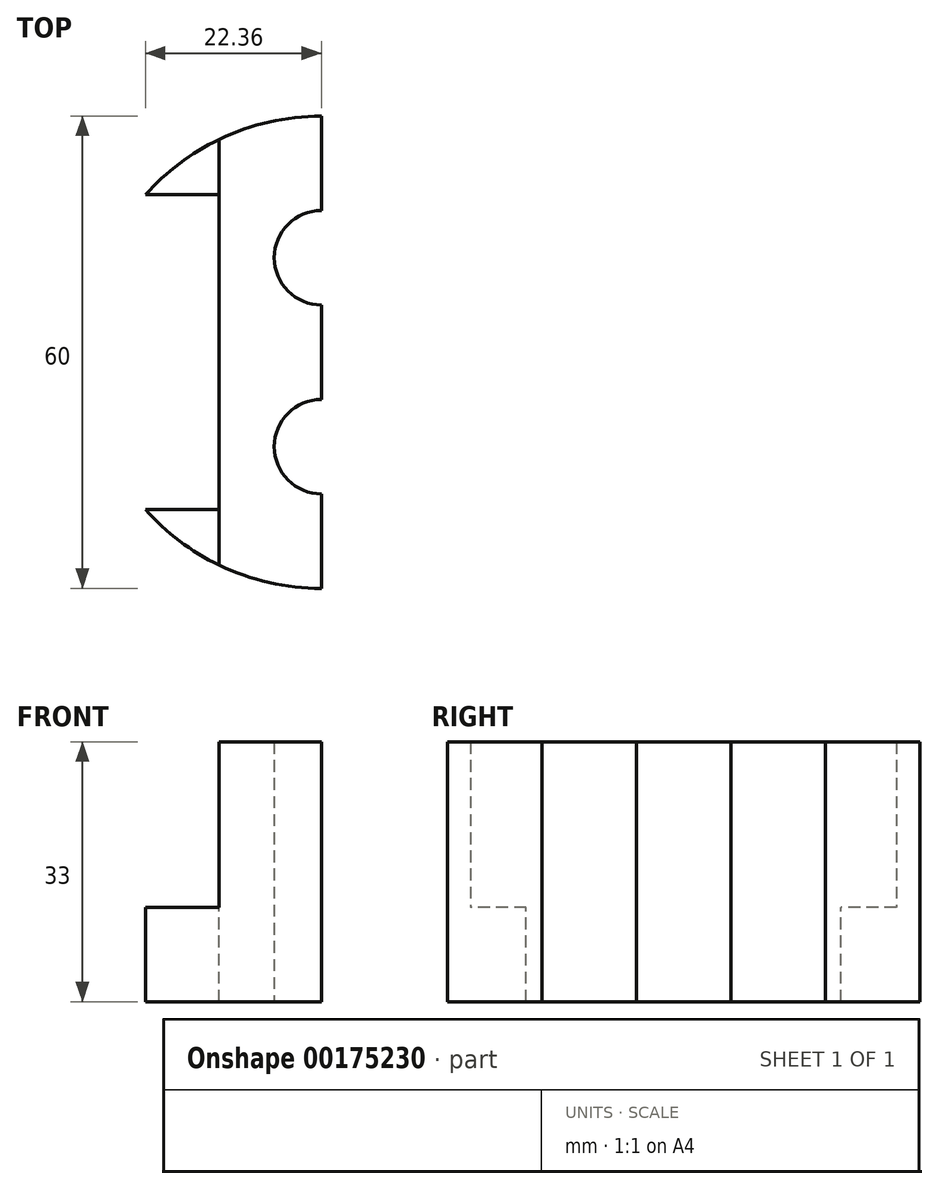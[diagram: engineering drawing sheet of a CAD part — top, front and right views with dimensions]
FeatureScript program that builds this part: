
annotation { "Feature Type Name" : "Feature", "Feature Type Description" : "" }
export const myFeature = defineFeature(function(context is Context, id is Id, definition is map)
    precondition{}
    {
        {
            var Q0;
            Q0=qCreatedBy(makeId("Top.planeOp"),FACE);
            var sketch = newSketch(context, id + "F0", { "sketchPlane" : qUnion([Q0])});
            skLineSegment(sketch, "E0.bottom", {"start": v(-13, -12) * mm, "end": v(13, -12) * mm});
            skLineSegment(sketch, "E0.top", {"start": v(-13, 12) * mm, "end": v(13, 12) * mm});
            skLineSegment(sketch, "E0.left", {"start": v(-13, -12) * mm, "end": v(-13, 12) * mm});
            skLineSegment(sketch, "E0.right", {"start": v(13, -12) * mm, "end": v(13, 12) * mm});
            skPoint(sketch, "E0.middle", {"position": v(0, 0) * mm});
            skCircle(sketch, "E1", {"center": v(0, 0) * mm, "radius": 20 * mm, "construction": true});
            skLineSegment(sketch, "E2", {"start": v(-31.1, 0) * mm, "end": v(39.02, 0) * mm, "construction": true});
            skCircle(sketch, "E3", {"center": v(0, 0) * mm, "radius": 30 * mm});
            skCircle(sketch, "E4", {"center": v(0, 12) * mm, "radius": 6 * mm});
            skCircle(sketch, "E5", {"center": v(0, -12) * mm, "radius": 6 * mm});
            skLineSegment(sketch, "E6.bottom", {"start": v(-13, 27.04) * mm, "end": v(13, 27.04) * mm});
            skLineSegment(sketch, "E6.top", {"start": v(-13, -27.04) * mm, "end": v(13, -27.04) * mm});
            skLineSegment(sketch, "E6.left", {"start": v(-13, 27.04) * mm, "end": v(-13, -27.04) * mm});
            skLineSegment(sketch, "E6.right", {"start": v(13, 27.04) * mm, "end": v(13, -27.04) * mm});
            skSolve(sketch);
        }
        {
            var Q0;
            {var subQ0=sQuery(id+"F0.wireOp",EDGE,"E6.bottom");Q0=makeQuery(id+"F0.imprint","IMPRINT",FACE,{"disambiguationData":[TD([[makeQuery(id+"F0.imprint","IMPRINT",EDGE,{"derivedFrom":subQ0}),1.0]])]});}
            var Q1;
            {var subQ0=sQuery(id+"F0.wireOp",EDGE,"E6.top");Q1=makeQuery(id+"F0.imprint","IMPRINT",FACE,{"disambiguationData":[TD([[makeQuery(id+"F0.imprint","IMPRINT",EDGE,{"derivedFrom":subQ0}),-1.0]])]});}
            var Q2;
            {var subQ0=sQuery(id+"F0.wireOp",EDGE,"E6.top");Q2=makeQuery(id+"F0.imprint","IMPRINT",FACE,{"disambiguationData":[TD([[makeQuery(id+"F0.imprint","IMPRINT",EDGE,{"derivedFrom":subQ0}),1.0]])]});}
            var Q3;
            {var subQ6=sQuery(id+"F0.wireOp",EDGE,"E0.bottom");var subQ9=sQuery(id+"F0.wireOp",EDGE,"E6.left");var subQ13=makeQuery(id+"F0.imprint","INTERSECT",VERTEX,{"derivedFrom":[subQ6,subQ9]});Q3=makeQuery(id+"F0.imprint","IMPRINT",FACE,{"disambiguationData":[TD([[makeQuery(id+"F0.imprint","IMPRINT",EDGE,{"disambiguationData":[TD([[subQ13,-1.0]])],"derivedFrom":subQ6}),1.0]])]});}
            var Q4;
            {var subQ0=sQuery(id+"F0.wireOp",EDGE,"E6.bottom");Q4=makeQuery(id+"F0.imprint","IMPRINT",FACE,{"disambiguationData":[TD([[makeQuery(id+"F0.imprint","IMPRINT",EDGE,{"derivedFrom":subQ0}),-1.0]])]});}
            extrude(context, id + "F1", {"entities" : qUnion([Q0, Q1, Q2, Q3, Q4]), "depth" : 33 * mm});
        }
        {
            var Q0;
            Q0=qCreatedBy(makeId("Top.planeOp"),FACE);
            var sketch = newSketch(context, id + "F2", { "sketchPlane" : qUnion([Q0])});
            skCircle(sketch, "E7", {"center": v(0, 0) * mm, "radius": 30 * mm});
            skCircle(sketch, "E8", {"center": v(-26.68, -13.72) * mm, "radius": 7.63 * mm});
            skLineSegment(sketch, "E9", {"start": v(-22.36, -20) * mm, "end": v(-12.88, -20) * mm});
            skLineSegment(sketch, "E10", {"start": v(-12.88, -20) * mm, "end": v(22.36, -20) * mm});
            skLineSegment(sketch, "E11", {"start": v(22.36, -20) * mm, "end": v(-53.5, 0) * mm, "construction": true});
            skLineSegment(sketch, "E12", {"start": v(-53.5, 0) * mm, "end": v(57.64, 0) * mm, "construction": true});
            skLineSegment(sketch, "E13.MirrorCS", {"start": v(-12.88, 20) * mm, "end": v(22.36, 20) * mm});
            skLineSegment(sketch, "E14.MirrorCS", {"start": v(-22.36, 20) * mm, "end": v(-12.88, 20) * mm});
            skSolve(sketch);
        }
        {
            var Q0;
            {var subQ0=sQuery(id+"F2.wireOp",EDGE,"E13.MirrorCS");Q0=makeQuery(id+"F2.imprint","IMPRINT",FACE,{"disambiguationData":[TD([[makeQuery(id+"F2.imprint","IMPRINT",EDGE,{"derivedFrom":subQ0}),1.0]])]});}
            var Q1;
            {var subQ0=sQuery(id+"F2.wireOp",EDGE,"E9");Q1=makeQuery(id+"F2.imprint","IMPRINT",FACE,{"disambiguationData":[TD([[makeQuery(id+"F2.imprint","IMPRINT",EDGE,{"derivedFrom":subQ0}),-1.0]])]});}
            extrude(context, id + "F3", {"entities" : qUnion([Q0, Q1]), "operationType" : NewBodyOperationType.ADD, "depth" : 12 * mm});
        }
        {
            var Q0;
            Q0=makeQuery(id+"F1.opExtrude","CAP_FACE",FACE,{"disambiguationData":[OSD([sQuery(id+"F0.wireOp",EDGE,"E3"),sQuery(id+"F0.wireOp",EDGE,"E4"),sQuery(id+"F0.wireOp",EDGE,"E5"),sQuery(id+"F0.wireOp",EDGE,"E6.left"),sQuery(id+"F0.wireOp",EDGE,"E6.right")])],"isStart":false});
            var sketch = newSketch(context, id + "F4", { "sketchPlane" : qUnion([Q0])});
            skLineSegment(sketch, "E15", {"start": v(0, 35.89) * mm, "end": v(0, -37.95) * mm});
            skPoint(sketch, "E15.endSnap0", {"position": v(0, 30) * mm});
            skLineSegment(sketch, "E16", {"start": v(0, -37.95) * mm, "end": v(28.6, -37.95) * mm});
            skLineSegment(sketch, "E17", {"start": v(28.6, -37.95) * mm, "end": v(28.6, 36.6) * mm});
            skLineSegment(sketch, "E18", {"start": v(28.6, 36.6) * mm, "end": v(0, 36.6) * mm});
            skLineSegment(sketch, "E19", {"start": v(0, 36.6) * mm, "end": v(0, 33.04) * mm});
            skSolve(sketch);
        }
        {
            var Q0;
            Q0=qSketchRegion(id+"F4",true);
            extrude(context, id + "F5", {"entities" : qUnion([Q0]), "operationType" : NewBodyOperationType.REMOVE, "endBound" : BoundingType.THROUGH_ALL, "oppositeDirection" : true, "depth" : 25 * mm});
        }
    });
